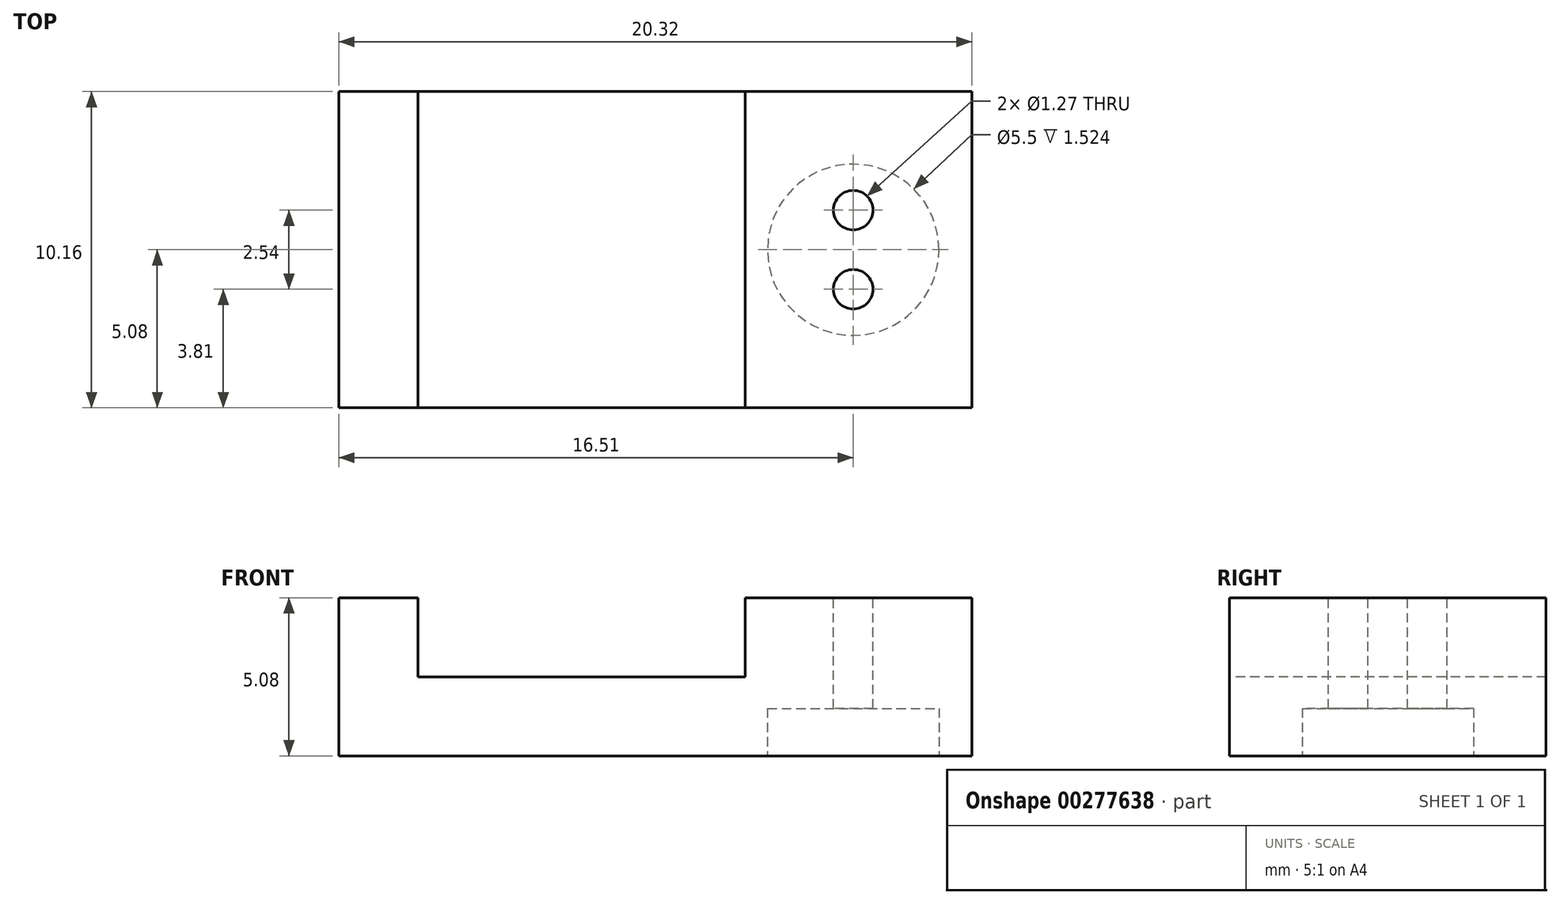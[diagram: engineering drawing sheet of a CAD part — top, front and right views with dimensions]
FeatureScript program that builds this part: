
annotation { "Feature Type Name" : "Feature", "Feature Type Description" : "" }
export const myFeature = defineFeature(function(context is Context, id is Id, definition is map)
    precondition{}
    {
        {
            var Q0;
            Q0=qCreatedBy(makeId("Top.planeOp"),FACE);
            var sketch = newSketch(context, id + "F0", { "sketchPlane" : qUnion([Q0])});
            skLineSegment(sketch, "E0.bottom", {"start": v(10.16, -5.08) * mm, "end": v(-10.16, -5.08) * mm});
            skLineSegment(sketch, "E0.top", {"start": v(10.16, 5.08) * mm, "end": v(-10.16, 5.08) * mm});
            skLineSegment(sketch, "E0.left", {"start": v(10.16, -5.08) * mm, "end": v(10.16, 5.08) * mm});
            skLineSegment(sketch, "E0.right", {"start": v(-10.16, -5.08) * mm, "end": v(-10.16, 5.08) * mm});
            skPoint(sketch, "E0.middle", {"position": v(0, 0) * mm});
            skSolve(sketch);
        }
        {
            var Q0;
            Q0=makeQuery(id+"F0.imprint","IMPRINT",FACE,{"disambiguationData":[TD([[makeQuery(id+"F0.imprint","IMPRINT",EDGE,{"derivedFrom":sQuery(id+"F0.wireOp",EDGE,"E0.bottom")}),-1.0]])]});
            extrude(context, id + "F1", {"entities" : qUnion([Q0]), "depth" : 5.08 * mm});
        }
        {
            var Q0;
            Q0=makeQuery(id+"F1.opExtrude","CAP_FACE",FACE,{"disambiguationData":[OSD([sQuery(id+"F0.wireOp",EDGE,"E0.bottom"),sQuery(id+"F0.wireOp",EDGE,"E0.top"),sQuery(id+"F0.wireOp",EDGE,"E0.left"),sQuery(id+"F0.wireOp",EDGE,"E0.right")])],"isStart":false});
            var sketch = newSketch(context, id + "F2", { "sketchPlane" : qUnion([Q0])});
            skLineSegment(sketch, "E1.bottom", {"start": v(-7.62, 5.08) * mm, "end": v(2.88, 5.08) * mm});
            skLineSegment(sketch, "E1.top", {"start": v(-7.62, -5.08) * mm, "end": v(2.88, -5.08) * mm});
            skLineSegment(sketch, "E1.left", {"start": v(-7.62, 5.08) * mm, "end": v(-7.62, -5.08) * mm});
            skLineSegment(sketch, "E1.right", {"start": v(2.88, 5.08) * mm, "end": v(2.88, -5.08) * mm});
            skSolve(sketch);
        }
        {
            var Q0;
            Q0=makeQuery(id+"F2.imprint","IMPRINT",FACE,{"disambiguationData":[TD([[makeQuery(id+"F2.imprint","IMPRINT",EDGE,{"derivedFrom":sQuery(id+"F2.wireOp",EDGE,"E1.bottom")}),1.0]])]});
            extrude(context, id + "F3", {"entities" : qUnion([Q0]), "operationType" : NewBodyOperationType.REMOVE, "oppositeDirection" : true, "depth" : 2.54 * mm});
        }
        {
            var Q0;
            {var subQ0=sQuery(id+"F0.wireOp",EDGE,"E0.bottom");var subQ1=sQuery(id+"F0.wireOp",EDGE,"E0.top");var subQ2=sQuery(id+"F0.wireOp",EDGE,"E0.left");Q0=makeQuery(id+"F3.boolean.opBoolean","SPLIT",FACE,{"disambiguationData":[TD([makeQuery(id+"F1.opExtrude","SWEPT_FACE",FACE,{"disambiguationData":[OSD([subQ2])]})])],"derivedFrom":makeQuery(id+"F1.opExtrude","CAP_FACE",FACE,{"disambiguationData":[OSD([subQ0,subQ1,subQ2,sQuery(id+"F0.wireOp",EDGE,"E0.right")])],"isStart":false})});}
            var sketch = newSketch(context, id + "F4", { "sketchPlane" : qUnion([Q0])});
            skPoint(sketch, "E2", {"position": v(6.35, 1.27) * mm});
            skPoint(sketch, "E3", {"position": v(6.35, -1.27) * mm});
            skSolve(sketch);
        }
        {
            var Q0;
            Q0=sQuery(id+"F4.wireOp",VERTEX,"E2");
            var Q1;
            Q1=sQuery(id+"F4.wireOp",VERTEX,"E3");
            var Q2;
            Q2=makeQuery(id+"F1.opExtrude","SWEPT_BODY",BODY,{"disambiguationData":[OSD([sQuery(id+"F0.wireOp",EDGE,"E0.bottom"),sQuery(id+"F0.wireOp",EDGE,"E0.top"),sQuery(id+"F0.wireOp",EDGE,"E0.left"),sQuery(id+"F0.wireOp",EDGE,"E0.right")])]});
            hole(context, id + "F5", {"style" : HoleStyle.SIMPLE, "endStyle" : HoleEndStyle.THROUGH, "holeDiameter" : 1.27 * mm, "tappedDepth" : 12.7 * mm, "tapClearance" : 3, "startFromSketch" : true, "locations" : qUnion([Q0, Q1]), "scope" : qUnion([Q2])});
        }
        {
            var Q0;
            Q0=makeQuery(id+"F1.opExtrude","CAP_FACE",FACE,{"disambiguationData":[OSD([sQuery(id+"F0.wireOp",EDGE,"E0.bottom"),sQuery(id+"F0.wireOp",EDGE,"E0.top"),sQuery(id+"F0.wireOp",EDGE,"E0.left"),sQuery(id+"F0.wireOp",EDGE,"E0.right")])],"isStart":true});
            var sketch = newSketch(context, id + "F6", { "sketchPlane" : qUnion([Q0])});
            skPoint(sketch, "E4", {"position": v(6.35, 0) * mm});
            skSolve(sketch);
        }
        {
            var Q0;
            {var subQ3=sQuery(id+"F0.wireOp",EDGE,"E0.bottom");Q0=makeQuery(id+"F6.imprint","IMPRINT",FACE,{"disambiguationData":[TD([[makeQuery(id+"F6.imprint","IMPRINT",EDGE,{"derivedFrom":makeQuery(id+"F1.opExtrude","CAP_EDGE",EDGE,{"disambiguationData":[OSD([subQ3])],"isStart":true})}),1.0]])]});}
            var sketch = newSketch(context, id + "F7", { "sketchPlane" : qUnion([Q0])});
            skCircle(sketch, "E5", {"center": v(6.35, 0) * mm, "radius": 2.75 * mm});
            skSolve(sketch);
        }
        {
            var Q0;
            Q0=makeQuery(id+"F7.imprint","IMPRINT",FACE,{"disambiguationData":[TD([[makeQuery(id+"F7.imprint","IMPRINT",EDGE,{"derivedFrom":sQuery(id+"F7.wireOp",EDGE,"E5")}),1.0]])]});
            extrude(context, id + "F8", {"entities" : qUnion([Q0]), "operationType" : NewBodyOperationType.REMOVE, "oppositeDirection" : true, "depth" : 1.52 * mm});
        }
    });
